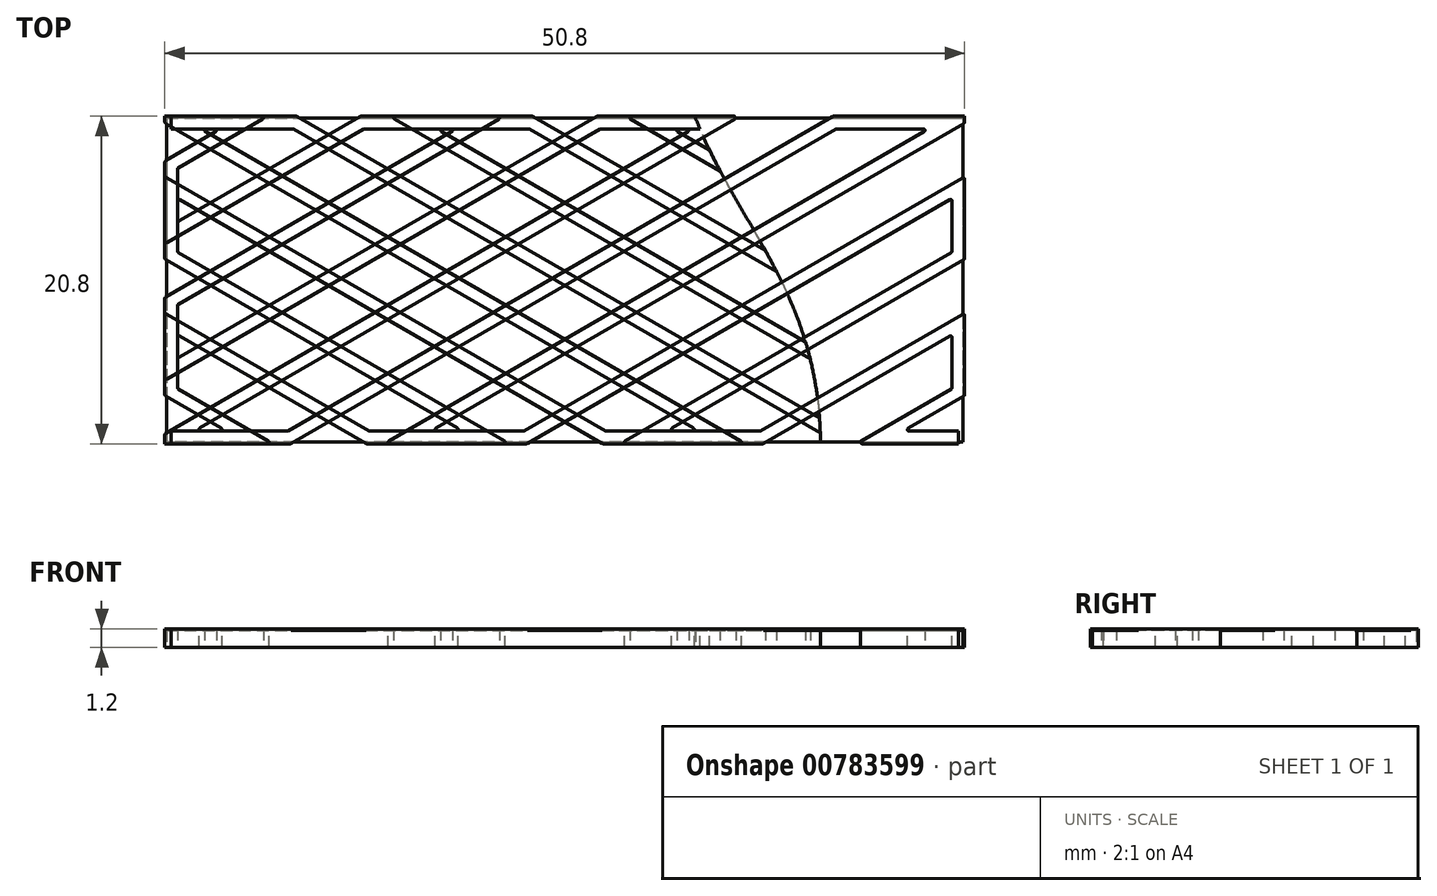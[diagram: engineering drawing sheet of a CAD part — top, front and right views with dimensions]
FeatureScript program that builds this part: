
annotation { "Feature Type Name" : "Feature", "Feature Type Description" : "" }
export const myFeature = defineFeature(function(context is Context, id is Id, definition is map)
    precondition{}
    {
        {
            var Q0;
            Q0=qCreatedBy(makeId("Top.planeOp"),FACE);
            var sketch = newSketch(context, id + "F0", { "sketchPlane" : qUnion([Q0])});
            skLineSegment(sketch, "E0.bottom", {"start": v(0, 0) * mm, "end": v(50, 0) * mm});
            skLineSegment(sketch, "E0.top", {"start": v(0, 20) * mm, "end": v(50, 20) * mm});
            skLineSegment(sketch, "E0.left", {"start": v(0, 0) * mm, "end": v(0, 20) * mm});
            skLineSegment(sketch, "E0.right", {"start": v(50, 0) * mm, "end": v(50, 20) * mm});
            skLineSegment(sketch, "E1", {"start": v(25, 36.98) * mm, "end": v(25, -17.72) * mm, "construction": true});
            skPoint(sketch, "E1.startSnap0", {"position": v(25, 20) * mm});
            skSolve(sketch);
        }
        {
            var Q0;
            Q0=sQuery(id+"F0.wireOp",EDGE,"E1");
            cPlane(context, id + "F1", {"entities" : qUnion([Q0]), "cplaneType" : CPlaneType.LINE_ANGLE, "offset" : 25 * mm, "angle" : 90 * degree, "width" : 150 * mm, "height" : 150 * mm});
        }
        {
            var Q0;
            Q0=qCreatedBy(makeId("Top.planeOp"),FACE);
            var sketch = newSketch(context, id + "F2", { "sketchPlane" : qUnion([Q0])});
            skLineSegment(sketch, "E2", {"start": v(0, 0) * mm, "end": v(34.64, 20) * mm});
            skLineSegment(sketch, "E3.1.0.0", {"start": v(7.5, 0) * mm, "end": v(42.14, 20) * mm});
            skLineSegment(sketch, "E3.2.0.0", {"start": v(15, 0) * mm, "end": v(49.64, 20) * mm});
            skLineSegment(sketch, "E3.3.0.0", {"start": v(22.5, 0) * mm, "end": v(50, 15.88) * mm});
            skLineSegment(sketch, "E3.4.0.0", {"start": v(30, 0) * mm, "end": v(50, 11.55) * mm});
            skLineSegment(sketch, "E3.5.0.0", {"start": v(37.5, 0) * mm, "end": v(50, 7.22) * mm});
            skLineSegment(sketch, "E3.6.0.0", {"start": v(45, 0) * mm, "end": v(50, 2.89) * mm});
            skLineSegment(sketch, "E4.1.0.0", {"start": v(0, 4.33) * mm, "end": v(27.14, 20) * mm});
            skLineSegment(sketch, "E4.2.0.0", {"start": v(0, 8.66) * mm, "end": v(19.64, 20) * mm});
            skLineSegment(sketch, "E4.3.0.0", {"start": v(0, 13) * mm, "end": v(12.14, 20) * mm});
            skLineSegment(sketch, "E4.4.0.0", {"start": v(0, 17.32) * mm, "end": v(4.64, 20) * mm});
            skLineSegment(sketch, "E5", {"start": v(0, 0) * mm, "end": v(7.5, 0) * mm});
            skLineSegment(sketch, "E6.1.0.0", {"start": v(15, 0) * mm, "end": v(22.5, 0) * mm});
            skLineSegment(sketch, "E6.2.0.0", {"start": v(30, 0) * mm, "end": v(37.5, 0) * mm});
            skLineSegment(sketch, "E6.3.0.0", {"start": v(45, 0) * mm, "end": v(50, 0) * mm});
            skLineSegment(sketch, "E7", {"start": v(0, 20) * mm, "end": v(4.64, 20) * mm});
            skLineSegment(sketch, "E8.1.0.0", {"start": v(12.14, 20) * mm, "end": v(19.64, 20) * mm});
            skLineSegment(sketch, "E8.2.0.0", {"start": v(27.14, 20) * mm, "end": v(34.64, 20) * mm});
            skLineSegment(sketch, "E8.3.0.0", {"start": v(42.14, 20) * mm, "end": v(49.64, 20) * mm});
            skPoint(sketch, "E9.orphan", {"position": v(-2.86, 20) * mm});
            skPoint(sketch, "E10.orphan", {"position": v(52.5, 0) * mm});
            skLineSegment(sketch, "E11", {"start": v(0, 4.33) * mm, "end": v(0, 8.66) * mm});
            skLineSegment(sketch, "E12", {"start": v(0, 13) * mm, "end": v(0, 17.32) * mm});
            skLineSegment(sketch, "E13", {"start": v(50, 15.88) * mm, "end": v(50, 11.55) * mm});
            skLineSegment(sketch, "E14", {"start": v(50, 7.22) * mm, "end": v(50, 2.89) * mm});
            skSolve(sketch);
        }
        {
            var Q0;
            Q0=sQuery(id+"F2.wireOp",VERTEX,"E7.start");
            var Q1;
            Q1=sQuery(id+"F2.wireOp",EDGE,"E7");
            cPlane(context, id + "F3", {"entities" : qUnion([Q0, Q1]), "cplaneType" : CPlaneType.LINE_POINT, "offset" : 25 * mm, "width" : 150 * mm, "height" : 150 * mm});
        }
        {
            var Q0;
            Q0=qCreatedBy(id+"F3.planeOp",FACE);
            var sketch = newSketch(context, id + "F4", { "sketchPlane" : qUnion([Q0])});
            skPoint(sketch, "E15.0", {"position": v(20, 0) * mm});
            skLineSegment(sketch, "E16", {"start": v(20, 0) * mm, "end": v(20.4, 0) * mm});
            skLineSegment(sketch, "E17", {"start": v(20.4, 0) * mm, "end": v(20.4, 1.2) * mm});
            skLineSegment(sketch, "E18", {"start": v(20.4, 1.2) * mm, "end": v(20, 1.2) * mm});
            skLineSegment(sketch, "E19", {"start": v(20, -0.76) * mm, "end": v(20, 2.5) * mm, "construction": true});
            skLineSegment(sketch, "E20.MirrorCS", {"start": v(19.6, 1.2) * mm, "end": v(20, 1.2) * mm});
            skLineSegment(sketch, "E21.MirrorCS", {"start": v(20, 0) * mm, "end": v(19.6, 0) * mm});
            skLineSegment(sketch, "E22.MirrorCS", {"start": v(19.6, 0) * mm, "end": v(19.6, 1.2) * mm});
            skSolve(sketch);
        }
        {
            var Q0;
            Q0=qSketchRegion(id+"F4",true);
            var Q1;
            Q1=sQuery(id+"F2.wireOp",EDGE,"E7");
            var Q2;
            Q2=sQuery(id+"F2.wireOp",EDGE,"E4.4.0.0");
            var Q3;
            Q3=sQuery(id+"F2.wireOp",EDGE,"E12");
            var Q4;
            Q4=sQuery(id+"F2.wireOp",EDGE,"E4.3.0.0");
            var Q5;
            Q5=sQuery(id+"F2.wireOp",EDGE,"E8.1.0.0");
            var Q6;
            Q6=sQuery(id+"F2.wireOp",EDGE,"E4.2.0.0");
            var Q7;
            Q7=sQuery(id+"F2.wireOp",EDGE,"E11");
            var Q8;
            Q8=sQuery(id+"F2.wireOp",EDGE,"E4.1.0.0");
            var Q9;
            Q9=sQuery(id+"F2.wireOp",EDGE,"E8.2.0.0");
            var Q10;
            Q10=sQuery(id+"F2.wireOp",EDGE,"E2");
            var Q11;
            Q11=sQuery(id+"F2.wireOp",EDGE,"E5");
            var Q12;
            Q12=sQuery(id+"F2.wireOp",EDGE,"E3.1.0.0");
            var Q13;
            Q13=sQuery(id+"F2.wireOp",EDGE,"E3.2.0.0");
            var Q14;
            Q14=sQuery(id+"F2.wireOp",EDGE,"E8.3.0.0");
            var Q15;
            Q15=sQuery(id+"F2.wireOp",EDGE,"E6.1.0.0");
            var Q16;
            Q16=sQuery(id+"F2.wireOp",EDGE,"E3.3.0.0");
            var Q17;
            Q17=sQuery(id+"F2.wireOp",EDGE,"E13");
            var Q18;
            Q18=sQuery(id+"F2.wireOp",EDGE,"E3.4.0.0");
            var Q19;
            Q19=sQuery(id+"F2.wireOp",EDGE,"E6.2.0.0");
            var Q20;
            Q20=sQuery(id+"F2.wireOp",EDGE,"E3.5.0.0");
            var Q21;
            Q21=sQuery(id+"F2.wireOp",EDGE,"E14");
            var Q22;
            Q22=sQuery(id+"F2.wireOp",EDGE,"E3.6.0.0");
            var Q23;
            Q23=sQuery(id+"F2.wireOp",EDGE,"E6.3.0.0");
            sweep(context, id + "F5", {"profiles" : qUnion([Q0]), "path" : qUnion([Q1, Q2, Q3, Q4, Q5, Q6, Q7, Q8, Q9, Q10, Q11, Q12, Q13, Q14, Q15, Q16, Q17, Q18, Q19, Q20, Q21, Q22, Q23])});
        }
        {
            var Q0;
            Q0=qCreatedBy(makeId("Top.planeOp"),FACE);
            var sketch = newSketch(context, id + "F6", { "sketchPlane" : qUnion([Q0])});
            skLineSegment(sketch, "E23.0", {"start": v(-0.4, 8.9) * mm, "end": v(-0.4, 3.64) * mm});
            skLineSegment(sketch, "E24.0", {"start": v(0, 20.4) * mm, "end": v(6.13, 20.4) * mm});
            skLineSegment(sketch, "E25.0", {"start": v(28.5, -0.4) * mm, "end": v(37.6, -0.4) * mm});
            skLineSegment(sketch, "E26.0", {"start": v(50.4, 16.57) * mm, "end": v(50.4, 11.32) * mm});
            skLineSegment(sketch, "E27.bottom", {"start": v(-0.4, 20.4) * mm, "end": v(50.4, 20.4) * mm});
            skLineSegment(sketch, "E27.top", {"start": v(-0.4, -0.4) * mm, "end": v(50.4, -0.4) * mm});
            skLineSegment(sketch, "E27.left", {"start": v(-0.4, 20.4) * mm, "end": v(-0.4, -0.4) * mm});
            skLineSegment(sketch, "E27.right", {"start": v(50.4, 20.4) * mm, "end": v(50.4, -0.4) * mm});
            skLineSegment(sketch, "E28.bottom", {"start": v(-6.4, 28.18) * mm, "end": v(56.43, 28.18) * mm});
            skLineSegment(sketch, "E28.top", {"start": v(-6.4, -9.1) * mm, "end": v(56.43, -9.1) * mm});
            skLineSegment(sketch, "E28.left", {"start": v(-6.4, 28.18) * mm, "end": v(-6.4, -9.1) * mm});
            skLineSegment(sketch, "E28.right", {"start": v(56.43, 28.18) * mm, "end": v(56.43, -9.1) * mm});
            skSolve(sketch);
        }
        {
            var Q0;
            {var subQ1=sQuery(id+"F6.wireOp",EDGE,"E23.0");Q0=makeQuery(id+"F6.imprint","IMPRINT",FACE,{"disambiguationData":[TD([[makeQuery(id+"F6.imprint","IMPRINT",EDGE,{"derivedFrom":subQ1}),-1.0]])]});}
            extrude(context, id + "F7", {"entities" : qUnion([Q0]), "depth" : 25 * mm, "offsetDistance" : 25 * mm});
        }
        {
            var Q0;
            Q0=makeQuery(id+"F7.opExtrude","SWEPT_BODY",BODY,{"disambiguationData":[OSD([sQuery(id+"F6.wireOp",EDGE,"E23.0"),sQuery(id+"F6.wireOp",EDGE,"E24.0"),sQuery(id+"F6.wireOp",EDGE,"E25.0"),sQuery(id+"F6.wireOp",EDGE,"E26.0"),sQuery(id+"F6.wireOp",EDGE,"E27.bottom"),sQuery(id+"F6.wireOp",EDGE,"E27.top"),sQuery(id+"F6.wireOp",EDGE,"E27.left"),sQuery(id+"F6.wireOp",EDGE,"E27.right"),sQuery(id+"F6.wireOp",EDGE,"E28.bottom"),sQuery(id+"F6.wireOp",EDGE,"E28.top"),sQuery(id+"F6.wireOp",EDGE,"E28.left"),sQuery(id+"F6.wireOp",EDGE,"E28.right")])]});
            var Q1;
            Q1=makeQuery(id+"F5.opSweep","SWEPT_BODY",BODY,{"disambiguationData":[OSD([sQuery(id+"F2.wireOp",EDGE,"E3.1.0.0"),sQuery(id+"F4.wireOp",EDGE,"E16"),sQuery(id+"F4.wireOp",EDGE,"E17"),sQuery(id+"F4.wireOp",EDGE,"E18"),sQuery(id+"F4.wireOp",EDGE,"E20.MirrorCS"),sQuery(id+"F4.wireOp",EDGE,"E21.MirrorCS"),sQuery(id+"F4.wireOp",EDGE,"E22.MirrorCS")])]});
            booleanBodies(context, id + "F8", {"operationType" : BooleanOperationType.SUBTRACTION, "tools" : qUnion([Q0]), "targets" : qUnion([Q1])});
        }
        {
            var Q0;
            Q0=qCreatedBy(makeId("Top.planeOp"),FACE);
            var sketch = newSketch(context, id + "F9", { "sketchPlane" : qUnion([Q0])});
            skLineSegment(sketch, "E29.0", {"start": v(-0.3, 20.3) * mm, "end": v(50.3, 20.3) * mm});
            skLineSegment(sketch, "E29.1", {"start": v(-0.3, 20.3) * mm, "end": v(-0.3, -0.3) * mm});
            skLineSegment(sketch, "E29.2", {"start": v(-0.3, -0.3) * mm, "end": v(50.3, -0.3) * mm});
            skLineSegment(sketch, "E29.3", {"start": v(50.3, 20.3) * mm, "end": v(50.3, -0.3) * mm});
            skSolve(sketch);
        }
        {
            var Q0;
            Q0=qSketchRegion(id+"F9",true);
            extrude(context, id + "F10", {"entities" : qUnion([Q0]), "depth" : 1.1 * mm, "offsetDistance" : 25 * mm});
        }
        {
            var Q0;
            Q0=makeQuery(id+"F5.opSweep","MID_CAP_EDGE",EDGE,{"disambiguationData":[OSD([sQuery(id+"F2.wireOp",VERTEX,"E12.end"),sQuery(id+"F4.wireOp",EDGE,"E22.MirrorCS")])],"capPos":2.0});
            var Q1;
            Q1=makeQuery(id+"F5.opSweep","MID_CAP_EDGE",EDGE,{"disambiguationData":[OSD([sQuery(id+"F2.wireOp",VERTEX,"E4.4.0.0.end"),sQuery(id+"F4.wireOp",EDGE,"E22.MirrorCS")])],"capPos":1.0});
            var Q2;
            Q2=makeQuery(id+"F5.opSweep","MID_CAP_EDGE",EDGE,{"disambiguationData":[OSD([sQuery(id+"F2.wireOp",VERTEX,"E4.4.0.0.end"),sQuery(id+"F4.wireOp",EDGE,"E17")])],"capPos":1.0});
            var Q3;
            Q3=makeQuery(id+"F5.opSweep","MID_CAP_EDGE",EDGE,{"disambiguationData":[OSD([sQuery(id+"F2.wireOp",VERTEX,"E12.end"),sQuery(id+"F4.wireOp",EDGE,"E17")])],"capPos":2.0});
            var Q4;
            Q4=makeQuery(id+"F5.opSweep","MID_CAP_EDGE",EDGE,{"disambiguationData":[OSD([sQuery(id+"F2.wireOp",VERTEX,"E4.3.0.0.start"),sQuery(id+"F4.wireOp",EDGE,"E17")])],"capPos":3.0});
            var Q5;
            Q5=makeQuery(id+"F5.opSweep","MID_CAP_EDGE",EDGE,{"disambiguationData":[OSD([sQuery(id+"F2.wireOp",VERTEX,"E4.3.0.0.start"),sQuery(id+"F4.wireOp",EDGE,"E22.MirrorCS")])],"capPos":3.0});
            var Q6;
            Q6=makeQuery(id+"F5.opSweep","MID_CAP_EDGE",EDGE,{"disambiguationData":[OSD([sQuery(id+"F2.wireOp",VERTEX,"E8.1.0.0.start"),sQuery(id+"F4.wireOp",EDGE,"E22.MirrorCS")])],"capPos":4.0});
            var Q7;
            Q7=makeQuery(id+"F5.opSweep","MID_CAP_EDGE",EDGE,{"disambiguationData":[OSD([sQuery(id+"F2.wireOp",VERTEX,"E8.1.0.0.start"),sQuery(id+"F4.wireOp",EDGE,"E17")])],"capPos":4.0});
            var Q8;
            Q8=makeQuery(id+"F5.opSweep","MID_CAP_EDGE",EDGE,{"disambiguationData":[OSD([sQuery(id+"F2.wireOp",VERTEX,"E4.2.0.0.end"),sQuery(id+"F4.wireOp",EDGE,"E22.MirrorCS")])],"capPos":5.0});
            var Q9;
            Q9=makeQuery(id+"F5.opSweep","MID_CAP_EDGE",EDGE,{"disambiguationData":[OSD([sQuery(id+"F2.wireOp",VERTEX,"E4.2.0.0.end"),sQuery(id+"F4.wireOp",EDGE,"E17")])],"capPos":5.0});
            var Q10;
            Q10=makeQuery(id+"F5.opSweep","MID_CAP_EDGE",EDGE,{"disambiguationData":[OSD([sQuery(id+"F2.wireOp",VERTEX,"E8.2.0.0.start"),sQuery(id+"F4.wireOp",EDGE,"E17")])],"capPos":8.0});
            var Q11;
            Q11=makeQuery(id+"F5.opSweep","MID_CAP_EDGE",EDGE,{"disambiguationData":[OSD([sQuery(id+"F2.wireOp",VERTEX,"E11.end"),sQuery(id+"F4.wireOp",EDGE,"E22.MirrorCS")])],"capPos":6.0});
            var Q12;
            Q12=makeQuery(id+"F5.opSweep","MID_CAP_EDGE",EDGE,{"disambiguationData":[OSD([sQuery(id+"F2.wireOp",VERTEX,"E11.end"),sQuery(id+"F4.wireOp",EDGE,"E17")])],"capPos":6.0});
            var Q13;
            Q13=makeQuery(id+"F5.opSweep","MID_CAP_EDGE",EDGE,{"disambiguationData":[OSD([sQuery(id+"F2.wireOp",VERTEX,"E4.1.0.0.start"),sQuery(id+"F4.wireOp",EDGE,"E17")])],"capPos":7.0});
            var Q14;
            Q14=makeQuery(id+"F5.opSweep","MID_CAP_EDGE",EDGE,{"disambiguationData":[OSD([sQuery(id+"F2.wireOp",VERTEX,"E4.1.0.0.start"),sQuery(id+"F4.wireOp",EDGE,"E22.MirrorCS")])],"capPos":7.0});
            var Q15;
            Q15=makeQuery(id+"F5.opSweep","MID_CAP_EDGE",EDGE,{"disambiguationData":[OSD([sQuery(id+"F2.wireOp",VERTEX,"E8.2.0.0.start"),sQuery(id+"F4.wireOp",EDGE,"E22.MirrorCS")])],"capPos":8.0});
            var Q16;
            Q16=makeQuery(id+"F5.opSweep","MID_CAP_EDGE",EDGE,{"disambiguationData":[OSD([sQuery(id+"F2.wireOp",VERTEX,"E2.end"),sQuery(id+"F4.wireOp",EDGE,"E22.MirrorCS")])],"capPos":9.0});
            var Q17;
            Q17=makeQuery(id+"F5.opSweep","MID_CAP_EDGE",EDGE,{"disambiguationData":[OSD([sQuery(id+"F2.wireOp",VERTEX,"E2.end"),sQuery(id+"F4.wireOp",EDGE,"E17")])],"capPos":9.0});
            var Q18;
            Q18=makeQuery(id+"F5.opSweep","MID_CAP_EDGE",EDGE,{"disambiguationData":[OSD([sQuery(id+"F2.wireOp",VERTEX,"E8.3.0.0.start"),sQuery(id+"F4.wireOp",EDGE,"E17")])],"capPos":12.0});
            var Q19;
            Q19=makeQuery(id+"F8.opBoolean","INTERSECT",EDGE,{"derivedFrom":[makeQuery(id+"F5.opSweep","SWEPT_FACE",FACE,{"disambiguationData":[OSD([sQuery(id+"F2.wireOp",EDGE,"E2"),sQuery(id+"F4.wireOp",EDGE,"E22.MirrorCS")])]}),makeQuery(id+"F7.opExtrude","SWEPT_FACE",FACE,{"disambiguationData":[OSD([sQuery(id+"F6.wireOp",EDGE,"E23.0"),sQuery(id+"F6.wireOp",EDGE,"E27.left")])]})]});
            var Q20;
            Q20=makeQuery(id+"F5.opSweep","MID_CAP_EDGE",EDGE,{"disambiguationData":[OSD([sQuery(id+"F2.wireOp",VERTEX,"E5.start"),sQuery(id+"F4.wireOp",EDGE,"E17")])],"capPos":10.0});
            var Q21;
            Q21=makeQuery(id+"F8.opBoolean","COPY",EDGE,{"derivedFrom":makeQuery(id+"F7.opExtrude","SWEPT_EDGE",EDGE,{"disambiguationData":[OSD([sQuery(id+"F6.wireOp",EDGE,"E27.top"),sQuery(id+"F6.wireOp",EDGE,"E27.left")])]})});
            var Q22;
            Q22=makeQuery(id+"F5.opSweep","MID_CAP_EDGE",EDGE,{"disambiguationData":[OSD([sQuery(id+"F2.wireOp",VERTEX,"E3.1.0.0.start"),sQuery(id+"F4.wireOp",EDGE,"E17")])],"capPos":11.0});
            var Q23;
            Q23=makeQuery(id+"F5.opSweep","MID_CAP_EDGE",EDGE,{"disambiguationData":[OSD([sQuery(id+"F2.wireOp",VERTEX,"E3.1.0.0.start"),sQuery(id+"F4.wireOp",EDGE,"E22.MirrorCS")])],"capPos":11.0});
            var Q24;
            Q24=makeQuery(id+"F5.opSweep","MID_CAP_EDGE",EDGE,{"disambiguationData":[OSD([sQuery(id+"F2.wireOp",VERTEX,"E8.3.0.0.start"),sQuery(id+"F4.wireOp",EDGE,"E22.MirrorCS")])],"capPos":12.0});
            var Q25;
            Q25=makeQuery(id+"F5.opSweep","MID_CAP_EDGE",EDGE,{"disambiguationData":[OSD([sQuery(id+"F2.wireOp",VERTEX,"E8.3.0.0.end"),sQuery(id+"F4.wireOp",EDGE,"E22.MirrorCS")])],"capPos":13.0});
            var Q26;
            Q26=makeQuery(id+"F8.opBoolean","COPY",EDGE,{"derivedFrom":makeQuery(id+"F7.opExtrude","SWEPT_EDGE",EDGE,{"disambiguationData":[OSD([sQuery(id+"F6.wireOp",EDGE,"E27.bottom"),sQuery(id+"F6.wireOp",EDGE,"E27.right")])]})});
            var Q27;
            Q27=makeQuery(id+"F8.opBoolean","INTERSECT",EDGE,{"derivedFrom":[makeQuery(id+"F5.opSweep","SWEPT_FACE",FACE,{"disambiguationData":[OSD([sQuery(id+"F2.wireOp",EDGE,"E3.2.0.0"),sQuery(id+"F4.wireOp",EDGE,"E17")])]}),makeQuery(id+"F7.opExtrude","SWEPT_FACE",FACE,{"disambiguationData":[OSD([sQuery(id+"F6.wireOp",EDGE,"E26.0"),sQuery(id+"F6.wireOp",EDGE,"E27.right")])]})]});
            var Q28;
            Q28=makeQuery(id+"F5.opSweep","MID_CAP_EDGE",EDGE,{"disambiguationData":[OSD([sQuery(id+"F2.wireOp",VERTEX,"E13.start"),sQuery(id+"F4.wireOp",EDGE,"E17")])],"capPos":16.0});
            var Q29;
            Q29=makeQuery(id+"F5.opSweep","MID_CAP_EDGE",EDGE,{"disambiguationData":[OSD([sQuery(id+"F2.wireOp",VERTEX,"E13.start"),sQuery(id+"F4.wireOp",EDGE,"E22.MirrorCS")])],"capPos":16.0});
            var Q30;
            Q30=makeQuery(id+"F5.opSweep","MID_CAP_EDGE",EDGE,{"disambiguationData":[OSD([sQuery(id+"F2.wireOp",VERTEX,"E3.4.0.0.end"),sQuery(id+"F4.wireOp",EDGE,"E22.MirrorCS")])],"capPos":17.0});
            var Q31;
            Q31=makeQuery(id+"F5.opSweep","MID_CAP_EDGE",EDGE,{"disambiguationData":[OSD([sQuery(id+"F2.wireOp",VERTEX,"E3.4.0.0.end"),sQuery(id+"F4.wireOp",EDGE,"E17")])],"capPos":17.0});
            var Q32;
            Q32=makeQuery(id+"F5.opSweep","MID_CAP_EDGE",EDGE,{"disambiguationData":[OSD([sQuery(id+"F2.wireOp",VERTEX,"E6.2.0.0.start"),sQuery(id+"F4.wireOp",EDGE,"E22.MirrorCS")])],"capPos":18.0});
            var Q33;
            Q33=makeQuery(id+"F5.opSweep","MID_CAP_EDGE",EDGE,{"disambiguationData":[OSD([sQuery(id+"F2.wireOp",VERTEX,"E6.2.0.0.start"),sQuery(id+"F4.wireOp",EDGE,"E17")])],"capPos":18.0});
            var Q34;
            Q34=makeQuery(id+"F5.opSweep","MID_CAP_EDGE",EDGE,{"disambiguationData":[OSD([sQuery(id+"F2.wireOp",VERTEX,"E3.3.0.0.start"),sQuery(id+"F4.wireOp",EDGE,"E22.MirrorCS")])],"capPos":15.0});
            var Q35;
            Q35=makeQuery(id+"F5.opSweep","MID_CAP_EDGE",EDGE,{"disambiguationData":[OSD([sQuery(id+"F2.wireOp",VERTEX,"E6.1.0.0.start"),sQuery(id+"F4.wireOp",EDGE,"E22.MirrorCS")])],"capPos":14.0});
            var Q36;
            Q36=makeQuery(id+"F5.opSweep","MID_CAP_EDGE",EDGE,{"disambiguationData":[OSD([sQuery(id+"F2.wireOp",VERTEX,"E6.1.0.0.start"),sQuery(id+"F4.wireOp",EDGE,"E17")])],"capPos":14.0});
            var Q37;
            Q37=makeQuery(id+"F5.opSweep","MID_CAP_EDGE",EDGE,{"disambiguationData":[OSD([sQuery(id+"F2.wireOp",VERTEX,"E3.5.0.0.start"),sQuery(id+"F4.wireOp",EDGE,"E17")])],"capPos":19.0});
            var Q38;
            Q38=makeQuery(id+"F5.opSweep","MID_CAP_EDGE",EDGE,{"disambiguationData":[OSD([sQuery(id+"F2.wireOp",VERTEX,"E3.3.0.0.start"),sQuery(id+"F4.wireOp",EDGE,"E17")])],"capPos":15.0});
            var Q39;
            Q39=makeQuery(id+"F5.opSweep","MID_CAP_EDGE",EDGE,{"disambiguationData":[OSD([sQuery(id+"F2.wireOp",VERTEX,"E14.start"),sQuery(id+"F4.wireOp",EDGE,"E17")])],"capPos":20.0});
            var Q40;
            Q40=makeQuery(id+"F5.opSweep","MID_CAP_EDGE",EDGE,{"disambiguationData":[OSD([sQuery(id+"F2.wireOp",VERTEX,"E14.start"),sQuery(id+"F4.wireOp",EDGE,"E22.MirrorCS")])],"capPos":20.0});
            var Q41;
            Q41=makeQuery(id+"F5.opSweep","MID_CAP_EDGE",EDGE,{"disambiguationData":[OSD([sQuery(id+"F2.wireOp",VERTEX,"E3.5.0.0.start"),sQuery(id+"F4.wireOp",EDGE,"E22.MirrorCS")])],"capPos":19.0});
            var Q42;
            Q42=makeQuery(id+"F5.opSweep","MID_CAP_EDGE",EDGE,{"disambiguationData":[OSD([sQuery(id+"F2.wireOp",VERTEX,"E6.3.0.0.start"),sQuery(id+"F4.wireOp",EDGE,"E22.MirrorCS")])],"capPos":22.0});
            var Q43;
            Q43=makeQuery(id+"F5.opSweep","MID_CAP_EDGE",EDGE,{"disambiguationData":[OSD([sQuery(id+"F2.wireOp",VERTEX,"E3.6.0.0.end"),sQuery(id+"F4.wireOp",EDGE,"E17")])],"capPos":21.0});
            var Q44;
            Q44=makeQuery(id+"F5.opSweep","MID_CAP_EDGE",EDGE,{"disambiguationData":[OSD([sQuery(id+"F2.wireOp",VERTEX,"E6.3.0.0.start"),sQuery(id+"F4.wireOp",EDGE,"E17")])],"capPos":22.0});
            var Q45;
            Q45=makeQuery(id+"F5.opSweep","MID_CAP_EDGE",EDGE,{"disambiguationData":[OSD([sQuery(id+"F2.wireOp",VERTEX,"E3.6.0.0.end"),sQuery(id+"F4.wireOp",EDGE,"E22.MirrorCS")])],"capPos":21.0});
            fillet(context, id + "F11", {"entities" : qUnion([Q0, Q1, Q2, Q3, Q4, Q5, Q6, Q7, Q8, Q9, Q10, Q11, Q12, Q13, Q14, Q15, Q16, Q17, Q18, Q19, Q20, Q21, Q22, Q23, Q24, Q25, Q26, Q27, Q28, Q29, Q30, Q31, Q32, Q33, Q34, Q35, Q36, Q37, Q38, Q39, Q40, Q41, Q42, Q43, Q44, Q45]), "radius" : .1 * mm, "tangentPropagation" : true, "allowEdgeOverflow" : false});
        }
        {
            var Q0;
            Q0=makeQuery(id+"F10.opExtrude","SWEPT_BODY",BODY,{"disambiguationData":[OSD([sQuery(id+"F9.wireOp",EDGE,"E29.0"),sQuery(id+"F9.wireOp",EDGE,"E29.1"),sQuery(id+"F9.wireOp",EDGE,"E29.2"),sQuery(id+"F9.wireOp",EDGE,"E29.3")])]});
            var Q1;
            Q1=makeQuery(id+"F15.opBoolean","SPLIT",BODY,{"disambiguationData":[OD(0.0)],"derivedFrom":makeQuery(id+"F5.opSweep","SWEPT_BODY",BODY,{"disambiguationData":[OSD([sQuery(id+"F2.wireOp",EDGE,"E3.1.0.0"),sQuery(id+"F4.wireOp",EDGE,"E16"),sQuery(id+"F4.wireOp",EDGE,"E17"),sQuery(id+"F4.wireOp",EDGE,"E18"),sQuery(id+"F4.wireOp",EDGE,"E20.MirrorCS"),sQuery(id+"F4.wireOp",EDGE,"E21.MirrorCS"),sQuery(id+"F4.wireOp",EDGE,"E22.MirrorCS")])]})});
            var Q2;
            Q2=qCreatedBy(id+"F1.planeOp",FACE);
            mirror(context, id + "F12", {"entities" : qUnion([Q0, Q1]), "mirrorPlane" : qUnion([Q2])});
        }
        {
            var Q0;
            Q0=qCreatedBy(makeId("Top.planeOp"),FACE);
            var sketch = newSketch(context, id + "F13", { "sketchPlane" : qUnion([Q0])});
            skLineSegment(sketch, "E30.0", {"start": v(42.06, 20.4) * mm, "end": v(50.3, 20.4) * mm});
            skLineSegment(sketch, "E31.0", {"start": v(50.4, 16.4) * mm, "end": v(50.4, 11.37) * mm});
            skLineSegment(sketch, "E32.0", {"start": v(43.88, -0.4) * mm, "end": v(50, -0.4) * mm});
            skLineSegment(sketch, "E33.bottom", {"start": v(50.4, 20.4) * mm, "end": v(33.26, 20.4) * mm});
            skLineSegment(sketch, "E33.top", {"start": v(50.4, -0.4) * mm, "end": v(33.26, -0.4) * mm});
            skLineSegment(sketch, "E33.left", {"start": v(50.4, 20.4) * mm, "end": v(50.4, -0.4) * mm});
            skFitSpline(sketch, "E34", {"points": [v(33.26, 20.4) * mm, v(41.24, -0.4) * mm], "startDerivative": vector(7.98, -20.8) * mm, "endDerivative": vector(0.16, -28.55) * mm});
            skSolve(sketch);
        }
        {
            var Q0;
            Q0 = qSketchRegion(id + "F13", true);
            extrude(context, id + "F14", {"entities" : qUnion([Q0]), "depth" : 25 * mm, "offsetDistance" : 25 * mm});
        }
        {
            var Q0;
            Q0=makeQuery(id+"F14.opExtrude","SWEPT_BODY",BODY,{"disambiguationData":[OSD([sQuery(id+"F13.wireOp",EDGE,"E33.bottom"),sQuery(id+"F13.wireOp",EDGE,"E33.top"),sQuery(id+"F13.wireOp",EDGE,"E33.left"),sQuery(id+"F13.wireOp",EDGE,"E34")])]});
            var Q1;
            Q1=makeQuery(id+"F12.opPattern","COPY",BODY,{"derivedFrom":makeQuery(id+"F10.opExtrude","SWEPT_BODY",BODY,{"disambiguationData":[OSD([sQuery(id+"F9.wireOp",EDGE,"E29.0"),sQuery(id+"F9.wireOp",EDGE,"E29.1"),sQuery(id+"F9.wireOp",EDGE,"E29.2"),sQuery(id+"F9.wireOp",EDGE,"E29.3")])]}),"instanceName":"1"});
            var Q2;
            Q2=makeQuery(id+"F12.opPattern","COPY",BODY,{"derivedFrom":makeQuery(id+"F5.opSweep","SWEPT_BODY",BODY,{"disambiguationData":[OSD([sQuery(id+"F2.wireOp",EDGE,"E3.1.0.0"),sQuery(id+"F4.wireOp",EDGE,"E16"),sQuery(id+"F4.wireOp",EDGE,"E17"),sQuery(id+"F4.wireOp",EDGE,"E18"),sQuery(id+"F4.wireOp",EDGE,"E20.MirrorCS"),sQuery(id+"F4.wireOp",EDGE,"E21.MirrorCS"),sQuery(id+"F4.wireOp",EDGE,"E22.MirrorCS")])]}),"instanceName":"1"});
            booleanBodies(context, id + "F15", {"operationType" : BooleanOperationType.SUBTRACTION, "tools" : qUnion([Q0]), "targets" : qUnion([Q1, Q2])});
        }
    });
